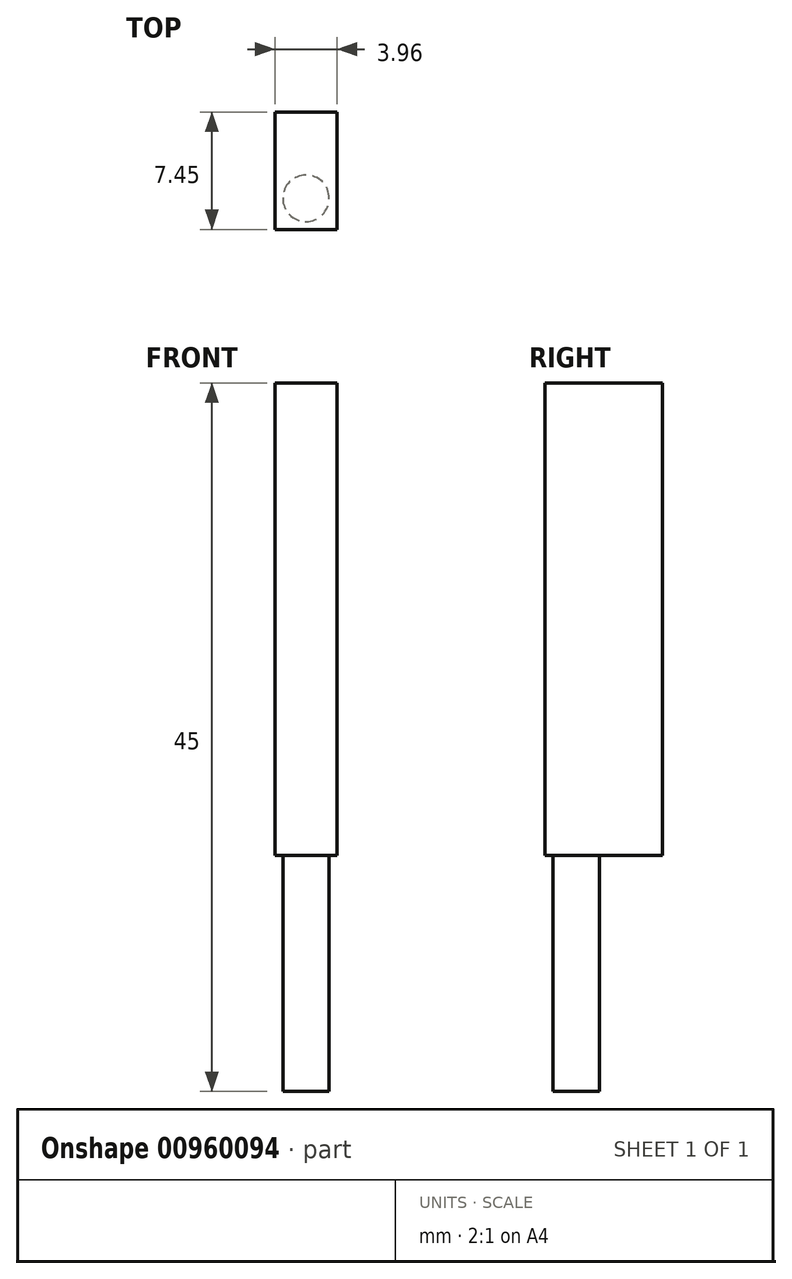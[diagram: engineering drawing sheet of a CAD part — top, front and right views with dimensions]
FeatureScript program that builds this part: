
annotation { "Feature Type Name" : "Feature", "Feature Type Description" : "" }
export const myFeature = defineFeature(function(context is Context, id is Id, definition is map)
    precondition{}
    {
        {
            var Q0;
            Q0=qCreatedBy(makeId("Top.planeOp"),FACE);
            var sketch = newSketch(context, id + "F0", { "sketchPlane" : qUnion([Q0])});
            skCircle(sketch, "E0", {"center": v(0, 0) * mm, "radius": 1.48 * mm});
            skSolve(sketch);
        }
        {
            var Q0;
            Q0=makeQuery(id+"F0.imprint","IMPRINT",FACE,{"disambiguationData":[TD([[makeQuery(id+"F0.imprint","IMPRINT",EDGE,{"derivedFrom":sQuery(id+"F0.wireOp",EDGE,"E0")}),1.0]])]});
            extrude(context, id + "F1", {"entities" : qUnion([Q0]), "depth" : 15 * mm, "offsetDistance" : 25 * mm});
        }
        {
            var Q0;
            Q0=makeQuery(id+"F1.opExtrude","CAP_FACE",FACE,{"disambiguationData":[OSD([sQuery(id+"F0.wireOp",EDGE,"E0")])],"isStart":false});
            var sketch = newSketch(context, id + "F2", { "sketchPlane" : qUnion([Q0])});
            skLineSegment(sketch, "E1.bottom", {"start": v(1.97, 5.48) * mm, "end": v(-1.98, 5.47) * mm});
            skLineSegment(sketch, "E1.top", {"start": v(1.98, -1.98) * mm, "end": v(-1.97, -1.98) * mm});
            skLineSegment(sketch, "E1.left", {"start": v(1.97, 5.48) * mm, "end": v(1.98, -1.98) * mm});
            skLineSegment(sketch, "E1.right", {"start": v(-1.98, 5.48) * mm, "end": v(-1.97, -1.98) * mm});
            skSolve(sketch);
        }
        {
            var Q0;
            Q0=makeQuery(id+"F2.imprint","IMPRINT",FACE,{"disambiguationData":[TD([[makeQuery(id+"F2.imprint","IMPRINT",EDGE,{"derivedFrom":sQuery(id+"F2.wireOp",EDGE,"E1.bottom")}),1.0]])]});
            var Q1;
            Q1=makeQuery(id+"F2.imprint","IMPRINT",FACE,{"disambiguationData":[TD([[makeQuery(id+"F2.imprint","IMPRINT",EDGE,{"derivedFrom":makeQuery(id+"F1.opExtrude","CAP_EDGE",EDGE,{"disambiguationData":[OSD([sQuery(id+"F0.wireOp",EDGE,"E0")])],"isStart":false})}),1.0]])]});
            extrude(context, id + "F3", {"entities" : qUnion([Q0, Q1]), "operationType" : NewBodyOperationType.ADD, "depth" : 30 * mm, "offsetDistance" : 25 * mm});
        }
    });
